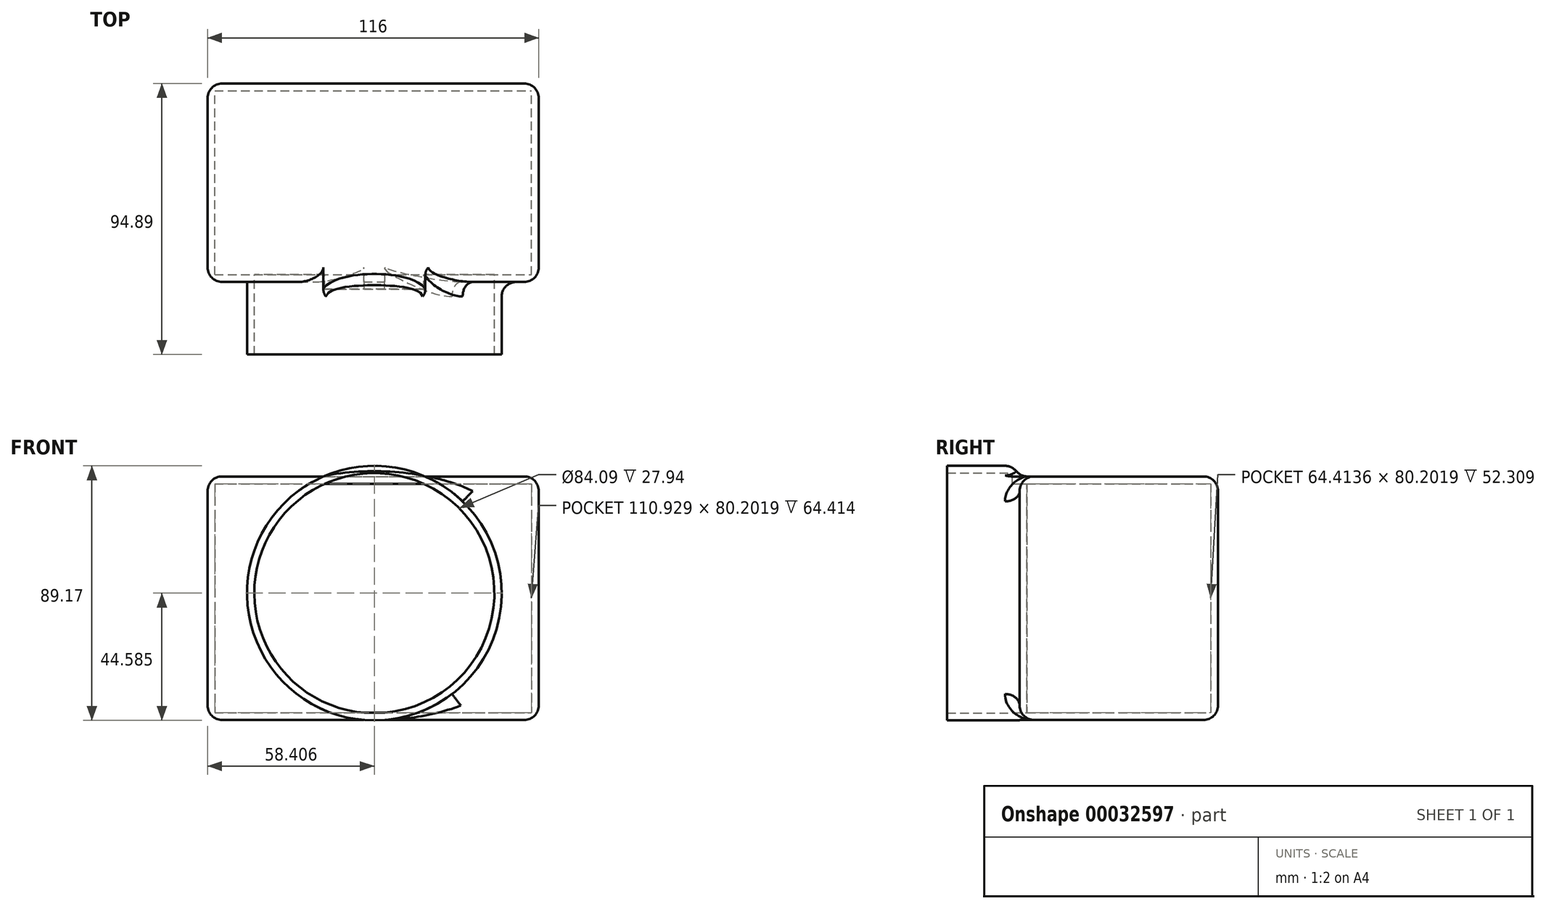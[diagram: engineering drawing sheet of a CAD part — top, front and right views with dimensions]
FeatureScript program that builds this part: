
annotation { "Feature Type Name" : "Feature", "Feature Type Description" : "" }
export const myFeature = defineFeature(function(context is Context, id is Id, definition is map)
    precondition{}
    {
        {
            var Q0;
            Q0=qCreatedBy(makeId("Front.planeOp"),FACE);
            var sketch = newSketch(context, id + "F0", { "sketchPlane" : qUnion([Q0])});
            skLineSegment(sketch, "E0.bottom", {"start": v(-71.12, 50.07) * mm, "end": v(44.88, 50.07) * mm});
            skLineSegment(sketch, "E0.top", {"start": v(-71.12, -35.2) * mm, "end": v(44.88, -35.2) * mm});
            skLineSegment(sketch, "E0.left", {"start": v(-71.12, 50.07) * mm, "end": v(-71.12, -35.2) * mm});
            skLineSegment(sketch, "E0.right", {"start": v(44.88, 50.07) * mm, "end": v(44.88, -35.2) * mm});
            skSolve(sketch);
        }
        {
            var Q0;
            Q0 = qSketchRegion(id + "F0", true);
            extrude(context, id + "F1", {"entities" : qUnion([Q0]), "depth" : 69.5 * mm});
        }
        {
            var Q0;
            Q0=makeQuery(id+"F1.opExtrude","CAP_FACE",FACE,{"disambiguationData":[OSD([sQuery(id+"F0.wireOp",EDGE,"E0.bottom"),sQuery(id+"F0.wireOp",EDGE,"E0.top"),sQuery(id+"F0.wireOp",EDGE,"E0.left"),sQuery(id+"F0.wireOp",EDGE,"E0.right")])],"isStart":false});
            var sketch = newSketch(context, id + "F2", { "sketchPlane" : qUnion([Q0])});
            skCircle(sketch, "E1", {"center": v(-12.71, 9.22) * mm, "radius": 44.58 * mm});
            skSolve(sketch);
        }
        {
            var Q0;
            Q0 = qSketchRegion(id + "F2", true);
            extrude(context, id + "F3", {"entities" : qUnion([Q0]), "operationType" : NewBodyOperationType.ADD, "depth" : 25.4 * mm});
        }
        {
            var Q0;
            Q0=makeQuery(id+"F3.opExtrude","CAP_FACE",FACE,{"disambiguationData":[OSD([sQuery(id+"F2.wireOp",EDGE,"E1")])],"isStart":false});
            shell(context, id + "F4", {"entities" : qUnion([Q0]), "thickness" : 2.54 * mm});
        }
        {
            var Q0;
            Q0=makeQuery(id+"F1.opExtrude","SWEPT_FACE",FACE,{"disambiguationData":[OSD([sQuery(id+"F0.wireOp",EDGE,"E0.top")])]});
            var Q1;
            Q1=makeQuery(id+"F1.opExtrude","SWEPT_FACE",FACE,{"disambiguationData":[OSD([sQuery(id+"F0.wireOp",EDGE,"E0.left")])]});
            var Q2;
            Q2=makeQuery(id+"F1.opExtrude","SWEPT_FACE",FACE,{"disambiguationData":[OSD([sQuery(id+"F0.wireOp",EDGE,"E0.bottom")])]});
            var Q3;
            Q3=makeQuery(id+"F1.opExtrude","SWEPT_FACE",FACE,{"disambiguationData":[OSD([sQuery(id+"F0.wireOp",EDGE,"E0.right")])]});
            fillet(context, id + "F5", {"entities" : qUnion([Q0, Q1, Q2, Q3]), "radius" : 5.08 * mm, "tangentPropagation" : true, "allowEdgeOverflow" : false});
        }
        {
            var Q0;
            {var subQ0=sQuery(id+"F2.wireOp",EDGE,"E1");Q0=makeQuery(id+"F3.boolean.opBoolean","SPLIT",EDGE,{"disambiguationData":[topologyDisambiguationEdgeConnected([makeQuery(id+"F1.opExtrude","CAP_FACE",FACE,{"disambiguationData":[OSD([sQuery(id+"F0.wireOp",EDGE,"E0.bottom"),sQuery(id+"F0.wireOp",EDGE,"E0.top"),sQuery(id+"F0.wireOp",EDGE,"E0.left"),sQuery(id+"F0.wireOp",EDGE,"E0.right")])],"isStart":false}),makeQuery(id+"F3.opExtrude","SWEPT_FACE",FACE,{"disambiguationData":[OSD([subQ0])]})]),OD(1.0)],"derivedFrom":makeQuery(id+"F3.opExtrude","CAP_EDGE",EDGE,{"disambiguationData":[OSD([subQ0])],"isStart":true})});}
            var Q1;
            {var subQ0=sQuery(id+"F2.wireOp",EDGE,"E1");Q1=makeQuery(id+"F3.boolean.opBoolean","SPLIT",EDGE,{"disambiguationData":[topologyDisambiguationEdgeConnected([makeQuery(id+"F1.opExtrude","CAP_FACE",FACE,{"disambiguationData":[OSD([sQuery(id+"F0.wireOp",EDGE,"E0.bottom"),sQuery(id+"F0.wireOp",EDGE,"E0.top"),sQuery(id+"F0.wireOp",EDGE,"E0.left"),sQuery(id+"F0.wireOp",EDGE,"E0.right")])],"isStart":false}),makeQuery(id+"F3.opExtrude","SWEPT_FACE",FACE,{"disambiguationData":[OSD([subQ0])]})]),OD(0.0)],"derivedFrom":makeQuery(id+"F3.opExtrude","CAP_EDGE",EDGE,{"disambiguationData":[OSD([subQ0])],"isStart":true})});}
            fillet(context, id + "F6", {"entities" : qUnion([Q0, Q1]), "radius" : 5.08 * mm, "tangentPropagation" : true, "allowEdgeOverflow" : false});
        }
        {
            var Q0;
            {var subQ0=sQuery(id+"F0.wireOp",EDGE,"E0.bottom");var subQ1=sQuery(id+"F2.wireOp",EDGE,"E1");var subQ2=makeQuery(id+"F3.opExtrude","SWEPT_FACE",FACE,{"disambiguationData":[OSD([subQ1])]});var subQ3=makeQuery(id+"F3.opExtrude","CAP_FACE",FACE,{"disambiguationData":[OSD([subQ1])],"isStart":true});Q0=makeQuery(id+"F3.boolean.opBoolean","SPLIT",EDGE,{"disambiguationData":[topologyDisambiguationEdgeConnected([subQ2,subQ3]),TD([makeQuery(id+"F1.opExtrude","SWEPT_FACE",FACE,{"disambiguationData":[OSD([subQ0])]})])],"derivedFrom":makeQuery(id+"F3.opExtrude","CAP_EDGE",EDGE,{"disambiguationData":[OSD([subQ1])],"isStart":true})});}
            fillet(context, id + "F7", {"entities" : qUnion([Q0]), "radius" : 5.08 * mm, "tangentPropagation" : true, "allowEdgeOverflow" : false});
        }
        {
            var Q0;
            {var subQ0=sQuery(id+"F0.wireOp",EDGE,"E0.bottom");var subQ1=makeQuery(id+"F1.opExtrude","SWEPT_FACE",FACE,{"disambiguationData":[OSD([subQ0])]});var subQ2=sQuery(id+"F2.wireOp",EDGE,"E1");var subQ3=makeQuery(id+"F3.opExtrude","SWEPT_FACE",FACE,{"disambiguationData":[OSD([subQ2])]});var subQ4=makeQuery(id+"F3.opExtrude","CAP_FACE",FACE,{"disambiguationData":[OSD([subQ2])],"isStart":true});Q0=makeQuery(id+"F7.opFillet","BLEND_EDGE",EDGE,{"blendedFrom":[makeQuery(id+"F3.boolean.opBoolean","SPLIT",EDGE,{"disambiguationData":[topologyDisambiguationEdgeConnected([subQ3,subQ4]),TD([subQ1])],"derivedFrom":makeQuery(id+"F3.opExtrude","CAP_EDGE",EDGE,{"disambiguationData":[OSD([subQ2])],"isStart":true})}),subQ1],"blendedInto":[subQ1]});}
            fillet(context, id + "F8", {"entities" : qUnion([Q0]), "radius" : 5.08 * mm, "tangentPropagation" : true, "allowEdgeOverflow" : false});
        }
    });
